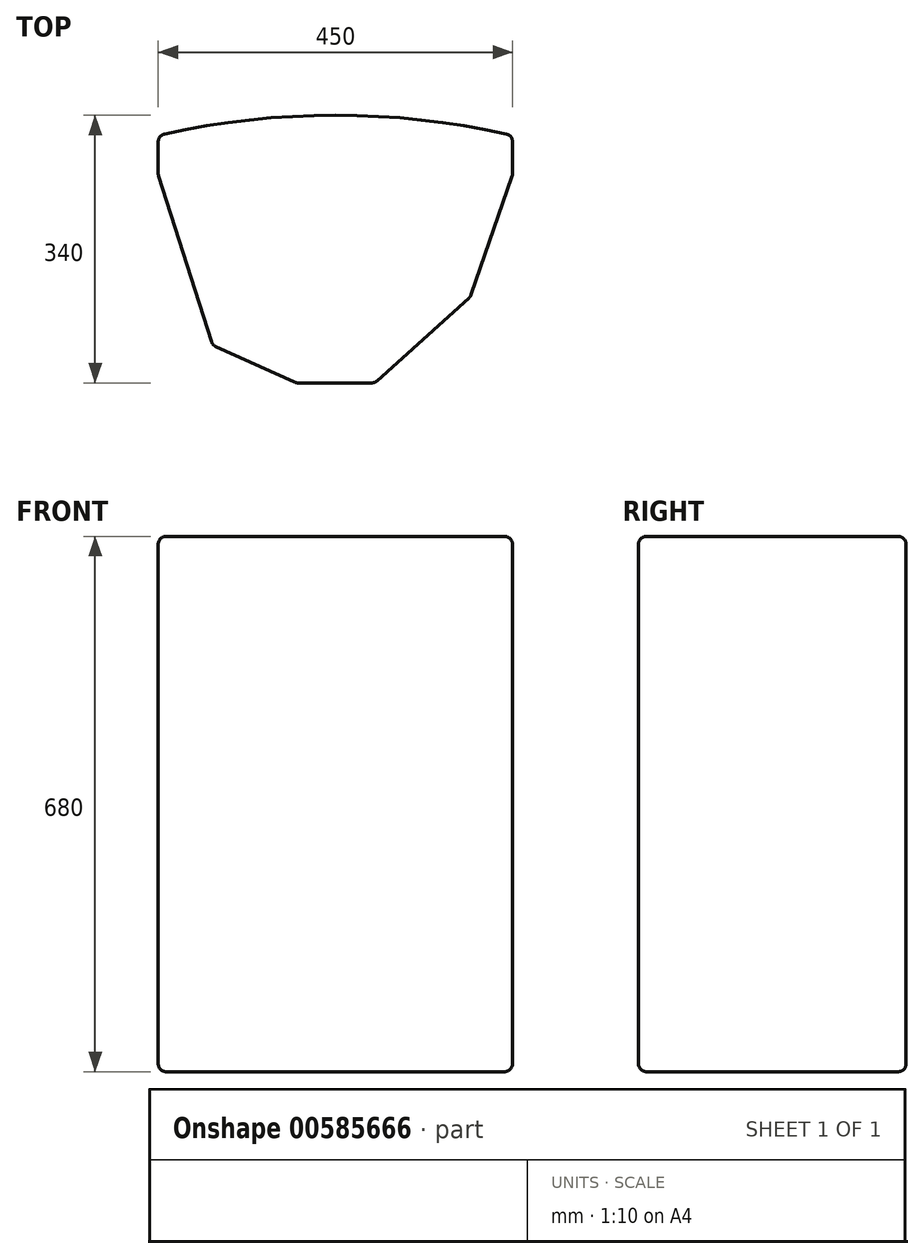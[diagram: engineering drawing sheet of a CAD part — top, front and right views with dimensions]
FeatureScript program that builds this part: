
annotation { "Feature Type Name" : "Feature", "Feature Type Description" : "" }
export const myFeature = defineFeature(function(context is Context, id is Id, definition is map)
    precondition{}
    {
        {
            var Q0;
            Q0=qCreatedBy(makeId("Top.planeOp"),FACE);
            var sketch = newSketch(context, id + "F0", { "sketchPlane" : qUnion([Q0])});
            skArc(sketch, "E0", {"start": v(225, 0) * mm, "mid": v(0, 25.64) * mm, "end": v(-225, 0) * mm});
            skLineSegment(sketch, "E1", {"start": v(-225, 0) * mm, "end": v(-225, -50) * mm});
            skLineSegment(sketch, "E2", {"start": v(-225, -50) * mm, "end": v(-156.18, -266.07) * mm});
            skLineSegment(sketch, "E3", {"start": v(-156.18, -266.07) * mm, "end": v(-50, -314.36) * mm});
            skLineSegment(sketch, "E4", {"start": v(-50, -314.36) * mm, "end": v(50, -314.36) * mm});
            skLineSegment(sketch, "E5", {"start": v(50, -314.36) * mm, "end": v(171.63, -204.77) * mm});
            skLineSegment(sketch, "E6", {"start": v(171.63, -204.77) * mm, "end": v(225, -50) * mm});
            skLineSegment(sketch, "E7", {"start": v(225, -50) * mm, "end": v(225, 0) * mm});
            skPoint(sketch, "E8", {"position": v(0, -314.36) * mm});
            skLineSegment(sketch, "E9", {"start": v(-225, 0) * mm, "end": v(166.72, -178.14) * mm, "construction": true});
            skLineSegment(sketch, "E10", {"start": v(166.72, -178.14) * mm, "end": v(225, -50) * mm, "construction": true});
            skSolve(sketch);
        }
        {
            var Q0;
            Q0 = qSketchRegion(id + "F0", true);
            extrude(context, id + "F1", {"entities" : qUnion([Q0]), "endBound" : BoundingType.SYMMETRIC, "depth" : 680 * mm, "offsetDistance" : 25 * mm});
        }
        {
            var Q0;
            Q0=makeQuery(id+"F1.opExtrude","SWEPT_FACE",FACE,{"disambiguationData":[OSD([sQuery(id+"F0.wireOp",EDGE,"E0")])]});
            var Q1;
            Q1=makeQuery(id+"F1.opExtrude","SWEPT_FACE",FACE,{"disambiguationData":[OSD([sQuery(id+"F0.wireOp",EDGE,"E1")])]});
            var Q2;
            Q2=makeQuery(id+"F1.opExtrude","SWEPT_FACE",FACE,{"disambiguationData":[OSD([sQuery(id+"F0.wireOp",EDGE,"E2")])]});
            var Q3;
            Q3=makeQuery(id+"F1.opExtrude","SWEPT_FACE",FACE,{"disambiguationData":[OSD([sQuery(id+"F0.wireOp",EDGE,"E7")])]});
            var Q4;
            Q4=makeQuery(id+"F1.opExtrude","SWEPT_FACE",FACE,{"disambiguationData":[OSD([sQuery(id+"F0.wireOp",EDGE,"E6")])]});
            var Q5;
            Q5=makeQuery(id+"F1.opExtrude","SWEPT_FACE",FACE,{"disambiguationData":[OSD([sQuery(id+"F0.wireOp",EDGE,"E5")])]});
            var Q6;
            Q6=makeQuery(id+"F1.opExtrude","SWEPT_FACE",FACE,{"disambiguationData":[OSD([sQuery(id+"F0.wireOp",EDGE,"E4")])]});
            var Q7;
            Q7=makeQuery(id+"F1.opExtrude","SWEPT_FACE",FACE,{"disambiguationData":[OSD([sQuery(id+"F0.wireOp",EDGE,"E3")])]});
            fillet(context, id + "F2", {"entities" : qUnion([Q0, Q1, Q2, Q3, Q4, Q5, Q6, Q7]), "radius" : 10 * mm, "tangentPropagation" : true, "allowEdgeOverflow" : false});
        }
    });
